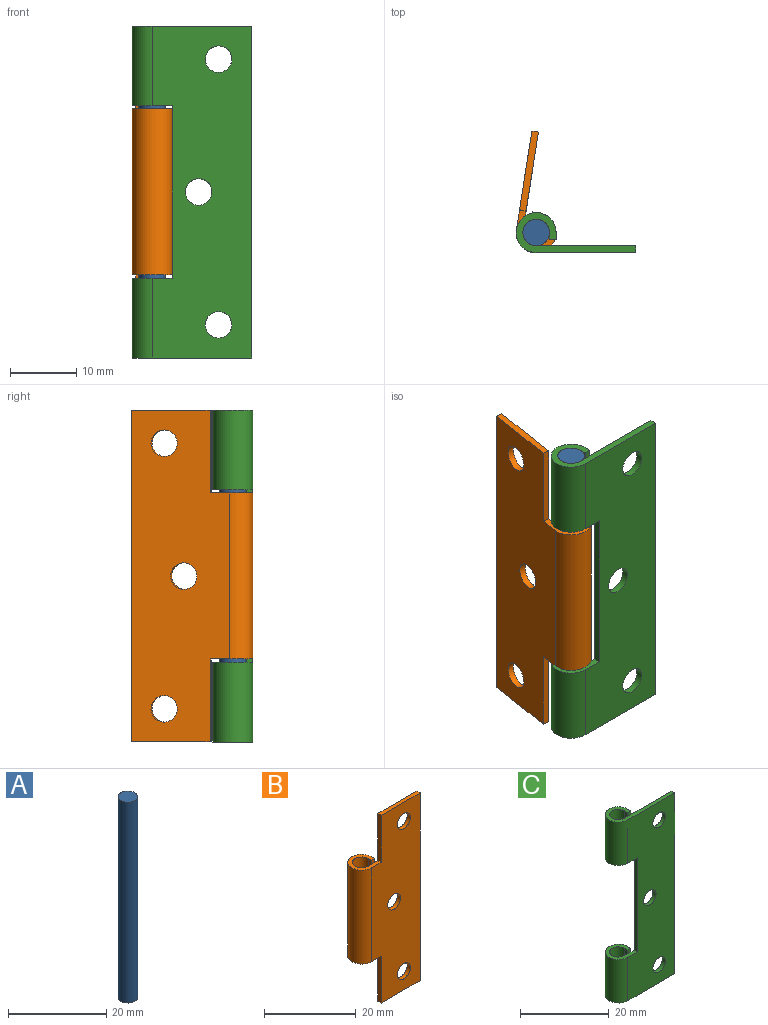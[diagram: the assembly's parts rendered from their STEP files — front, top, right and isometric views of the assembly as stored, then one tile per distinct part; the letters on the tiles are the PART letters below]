
ASSEMBLY  parts=3 mates=3
PART A: 3 faces, bbox 4x4x50 mm
  f0: cylinder r=2mm len=50mm, axis (0,0,-1), area 628.3mm2, adj f1,f2
  f1: plane 4x4mm, normal (0,0,1), area 12.6mm2, adj f0
  f2: plane 4x4mm, normal (0,0,-1), area 12.6mm2, adj f0
PART B: 17 faces, bbox 18x6x50 mm
  f0: plane 25x1mm, normal (1,0,0), area 25mm2, adj f2,f6,f13,f15
  f1: plane 50x15mm, normal (0,-1,0), area 637.3mm2, adj f2,f7,f8,f9,f10,f11,f12,f13
  f2: cylinder r=3mm len=25mm, axis (0,0,-1), area 353.4mm2, adj f0,f1,f13,f15
  f3: plane 50x15mm, normal (0,1,0), area 637.3mm2, adj f4,f7,f8,f9,f10,f11,f12,f13
  f4: cylinder r=2mm len=25mm, axis (0,0,-1), area 235.6mm2, adj f3,f5,f13,f15
  f5: plane 25x1mm, normal (-1,0,0), area 25mm2, adj f4,f6,f13,f15
  f6: plane 25x1mm, normal (0,-1,0), area 25mm2, adj f0,f5,f13,f15
  f7: plane 12x1mm, normal (0,0,1), area 12mm2, adj f1,f3,f9,f16
  f8: plane 12x1mm, normal (0,0,-1), area 12mm2, adj f1,f3,f9,f14
  f9: plane 50x1mm, normal (1,0,0), area 50mm2, adj f1,f3,f7,f8
  f10: cylinder r=2mm len=4mm, axis (0,-1,0), area 12.6mm2, adj f1,f3
  f11: cylinder r=2mm len=4mm, axis (0,-1,0), area 12.6mm2, adj f1,f3
  f12: cylinder r=2mm len=4mm, axis (0,-1,0), area 12.6mm2, adj f1,f3
  f13: plane 6x6mm, normal (0,0,-1), area 15.8mm2, adj f0,f1,f2,f3,f4,f5,f6,f14
  f14: plane 12.5x1mm, normal (-1,0,0), area 12.5mm2, adj f1,f3,f8,f13
  f15: plane 6x6mm, normal (0,0,1), area 15.8mm2, adj f0,f1,f2,f3,f4,f5,f6,f16
  f16: plane 12.5x1mm, normal (-1,0,0), area 12.5mm2, adj f1,f3,f7,f15
PART C: 21 faces, bbox 18x6x50 mm
  f0: plane 12x1mm, normal (1,0,0), area 12mm2, adj f3,f4,f13,f19
  f1: cylinder r=2mm len=12mm, axis (0,0,-1), area 113.1mm2, adj f2,f12,f13,f19
  f2: plane 12x1mm, normal (-1,0,0), area 12mm2, adj f1,f3,f13,f19
  f3: plane 12x1mm, normal (0,-1,0), area 12mm2, adj f0,f2,f13,f19
  f4: cylinder r=3mm len=12mm, axis (0,0,-1), area 169.6mm2, adj f0,f10,f13,f19
  f5: cylinder r=2mm len=12mm, axis (0,0,-1), area 113.1mm2, adj f6,f12,f14,f18
  f6: plane 12x1mm, normal (-1,0,0), area 12mm2, adj f5,f7,f14,f18
  f7: plane 12x1mm, normal (0,-1,0), area 12mm2, adj f6,f8,f14,f18
  f8: plane 12x1mm, normal (1,0,0), area 12mm2, adj f7,f9,f14,f18
  f9: cylinder r=3mm len=12mm, axis (0,0,-1), area 169.6mm2, adj f8,f10,f14,f18
  f10: plane 50x15mm, normal (0,-1,0), area 634.3mm2, adj f4,f9,f11,f13,f14,f15,f16,f17
  f11: plane 50x1mm, normal (1,0,0), area 50mm2, adj f10,f12,f13,f14
  f12: plane 50x15mm, normal (0,1,0), area 634.3mm2, adj f1,f5,f11,f13,f14,f15,f16,f17
  f13: plane 18x6mm, normal (0,0,1), area 27.8mm2, adj f0,f1,f2,f3,f4,f10,f11,f12
  f14: plane 18x6mm, normal (0,0,-1), area 27.8mm2, adj f5,f6,f7,f8,f9,f10,f11,f12
  f15: cylinder r=2mm len=4mm, axis (0,-1,0), area 12.6mm2, adj f10,f12
  f16: cylinder r=2mm len=4mm, axis (0,-1,0), area 12.6mm2, adj f10,f12
  f17: cylinder r=2mm len=4mm, axis (0,-1,0), area 12.6mm2, adj f10,f12
  f18: plane 6x6mm, normal (0,0,1), area 15.8mm2, adj f5,f6,f7,f8,f9,f10,f12,f20
  f19: plane 6x6mm, normal (0,0,-1), area 15.8mm2, adj f0,f1,f2,f3,f4,f10,f12,f20
  f20: plane 26x1mm, normal (-1,0,0), area 26mm2, adj f10,f12,f18,f19
PLACE A rot(axis=(0,0,-1),8.9deg) t=(-15,3,0)mm
PLACE B rot(axis=(-0.76,-0.65,0),180deg) t=(-17.96,3.46,50)mm
PLACE C t=(-15,0,0)mm
MATE fastened A.f0 <-> B.f2  axis (0,0,-1) through (-15,3,25)mm
MATE parallel B.f15 <-> C.f18  axis (0,0,-1) through (-15.1,3.06,12.5)mm
MATE cylindrical B.f2 <-> C.f1  axis (0,0,1) through (-15,3,25)mm
